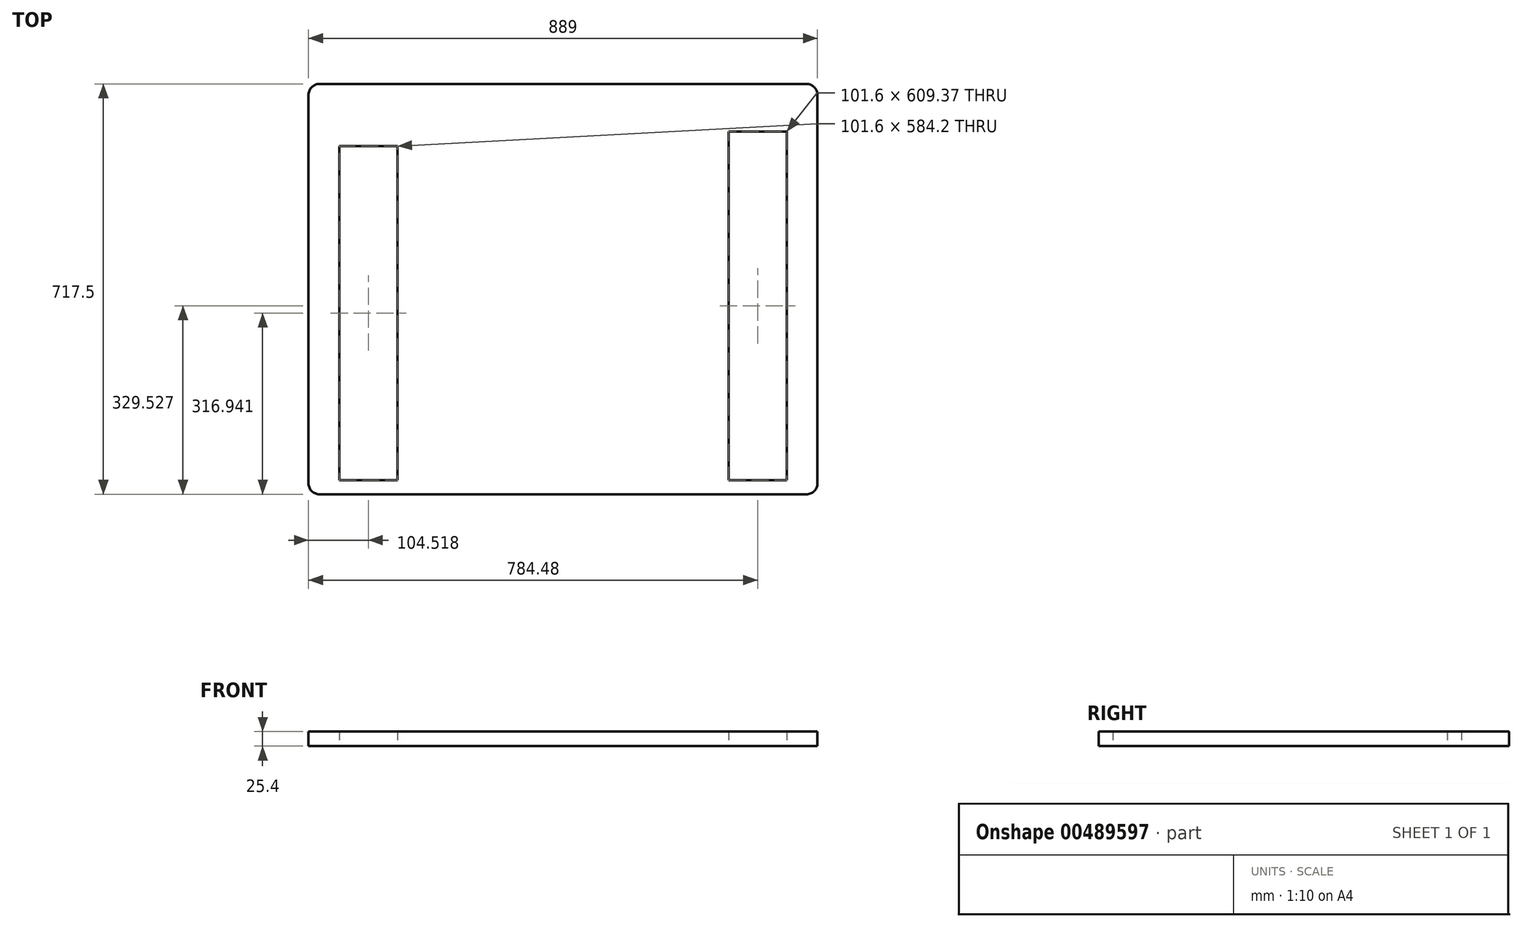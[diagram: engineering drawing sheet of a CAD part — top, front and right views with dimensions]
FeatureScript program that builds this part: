
annotation { "Feature Type Name" : "Feature", "Feature Type Description" : "" }
export const myFeature = defineFeature(function(context is Context, id is Id, definition is map)
    precondition{}
    {
        {
            var Q0;
            Q0=qCreatedBy(makeId("Top.planeOp"),FACE);
            var sketch = newSketch(context, id + "F0", { "sketchPlane" : qUnion([Q0])});
            skLineSegment(sketch, "E0.top", {"start": v(-438.56, -93.95) * mm, "end": v(412.34, -93.95) * mm});
            skLineSegment(sketch, "E0.left", {"start": v(-457.61, 458.5) * mm, "end": v(-457.61, -74.9) * mm});
            skLineSegment(sketch, "E0.right", {"start": v(431.39, 458.5) * mm, "end": v(431.39, -74.9) * mm});
            skLineSegment(sketch, "E1.top", {"start": v(314.17, -69.1) * mm, "end": v(377.67, -69.1) * mm});
            skLineSegment(sketch, "E1.right", {"start": v(377.67, 515.1) * mm, "end": v(377.67, -69.1) * mm});
            skLineSegment(sketch, "E2.top", {"start": v(-403.9, -69.1) * mm, "end": v(-340.4, -69.1) * mm});
            skPoint(sketch, "E3.visualSharp", {"position": v(-457.61, 477.55) * mm});
            skPoint(sketch, "E4.visualSharp", {"position": v(-457.61, -93.95) * mm});
            skArc(sketch, "E4.filletArc", {"start": v(-457.61, -74.9) * mm, "mid": v(-452.03, -88.37) * mm, "end": v(-438.56, -93.95) * mm});
            skPoint(sketch, "E5.visualSharp", {"position": v(431.39, 477.55) * mm});
            skPoint(sketch, "E6.visualSharp", {"position": v(431.39, -93.95) * mm});
            skArc(sketch, "E6.filletArc", {"start": v(412.34, -93.95) * mm, "mid": v(425.8, -88.37) * mm, "end": v(431.39, -74.9) * mm});
            skLineSegment(sketch, "E7", {"start": v(377.67, 540.26) * mm, "end": v(377.67, 515.1) * mm});
            skLineSegment(sketch, "E8", {"start": v(-340.4, -69.1) * mm, "end": v(-302.3, -69.1) * mm});
            skLineSegment(sketch, "E9", {"start": v(314.17, -69.1) * mm, "end": v(276.07, -69.1) * mm});
            skLineSegment(sketch, "E10", {"start": v(276.07, -69.1) * mm, "end": v(276.07, 438.66) * mm});
            skLineSegment(sketch, "E11", {"start": v(-403.9, 515.1) * mm, "end": v(-302.3, 515.1) * mm});
            skLineSegment(sketch, "E12", {"start": v(377.67, 540.26) * mm, "end": v(377.67, 483.53) * mm});
            skLineSegment(sketch, "E13", {"start": v(-457.61, 458.5) * mm, "end": v(-457.61, 604.5) * mm});
            skLineSegment(sketch, "E14", {"start": v(-438.56, 623.55) * mm, "end": v(412.34, 623.55) * mm});
            skLineSegment(sketch, "E15", {"start": v(431.39, 604.5) * mm, "end": v(431.39, 458.5) * mm});
            skPoint(sketch, "E16.visualSharp", {"position": v(-457.61, 623.55) * mm});
            skArc(sketch, "E16.filletArc", {"start": v(-438.56, 623.55) * mm, "mid": v(-452.03, 617.97) * mm, "end": v(-457.61, 604.5) * mm});
            skPoint(sketch, "E17.visualSharp", {"position": v(431.39, 623.55) * mm});
            skArc(sketch, "E17.filletArc", {"start": v(431.39, 604.5) * mm, "mid": v(425.8, 617.97) * mm, "end": v(412.34, 623.55) * mm});
            skPoint(sketch, "E18.end.orphan", {"position": v(-302.3, 438.66) * mm});
            skLineSegment(sketch, "E19", {"start": v(-403.9, 515.1) * mm, "end": v(-403.9, -69.1) * mm});
            skLineSegment(sketch, "E20", {"start": v(-302.3, -69.1) * mm, "end": v(-302.3, 515.1) * mm});
            skLineSegment(sketch, "E21", {"start": v(377.67, 540.26) * mm, "end": v(276.07, 540.26) * mm});
            skLineSegment(sketch, "E22", {"start": v(276.07, 540.26) * mm, "end": v(276.07, 438.66) * mm});
            skSolve(sketch);
        }
        {
            var Q0;
            Q0 = qSketchRegion(id + "F0", true);
            extrude(context, id + "F1", {"entities" : qUnion([Q0]), "depth" : 25.4 * mm, "offsetDistance" : 25.4 * mm});
        }
    });
